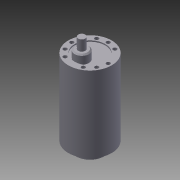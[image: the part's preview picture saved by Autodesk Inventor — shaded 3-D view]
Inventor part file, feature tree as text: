
AUTODESK INVENTOR PART (.ipt)
format: ipt  version: 2012 (Build 160160000, 160)  size: 136,704 bytes
history: native  units: mm
features: extrude x6, sketch x2, chamfer x1
ambient origin geometry x8: Origin, YZ Plane, XZ Plane, XY Plane, X Axis, Y Axis, Z Axis, Center Point
bodies: Solid1 (feature_tree)
feature tree (9):
  sketch  "Sketch1"  dims[d0=36.8mm d1=6.0mm]
  extrude  "Extrusion1"  Depth=6.0mm
  extrude  "Extrusion2"  Depth=64.516mm TaperAngle=0.0deg
  extrude  "Extrusion3"  Depth=6.5mm TaperAngle=0.0deg
  extrude  "Extrusion4"  Depth=15.5mm TaperAngle=0.0deg
  chamfer  "Chamfer1"  Distance=24.1mm
  extrude  "Extrusion5"  Depth=5.6mm TaperAngle=0.0deg
  extrude  "Extrusion6"  Depth=1.0mm TaperAngle=45.0deg
  sketch  "Sketch2"  dims[d3=12.0mm d4=64.516mm d5=0.0mm d6=6.5mm d7=0.0mm d8=15.5mm d9=0.0mm d10=24.1mm d11=5.6mm d12=0.0mm d13=1.0mm d14=2.0mm d15=45.0deg d16=3.2mm d17=15.5mm d19=8.02339mm d20=8.02339mm d21=8.02339mm d22=8.02339mm d25=31.0mm d26=31.0mm d27=31.0mm d28=15.5mm d29=15.5mm d30=8.02339mm d31=8.02339mm d32=7.0mm d33=1.0mm d34=0.0mm d35=10.0mm d36=0.0mm]
